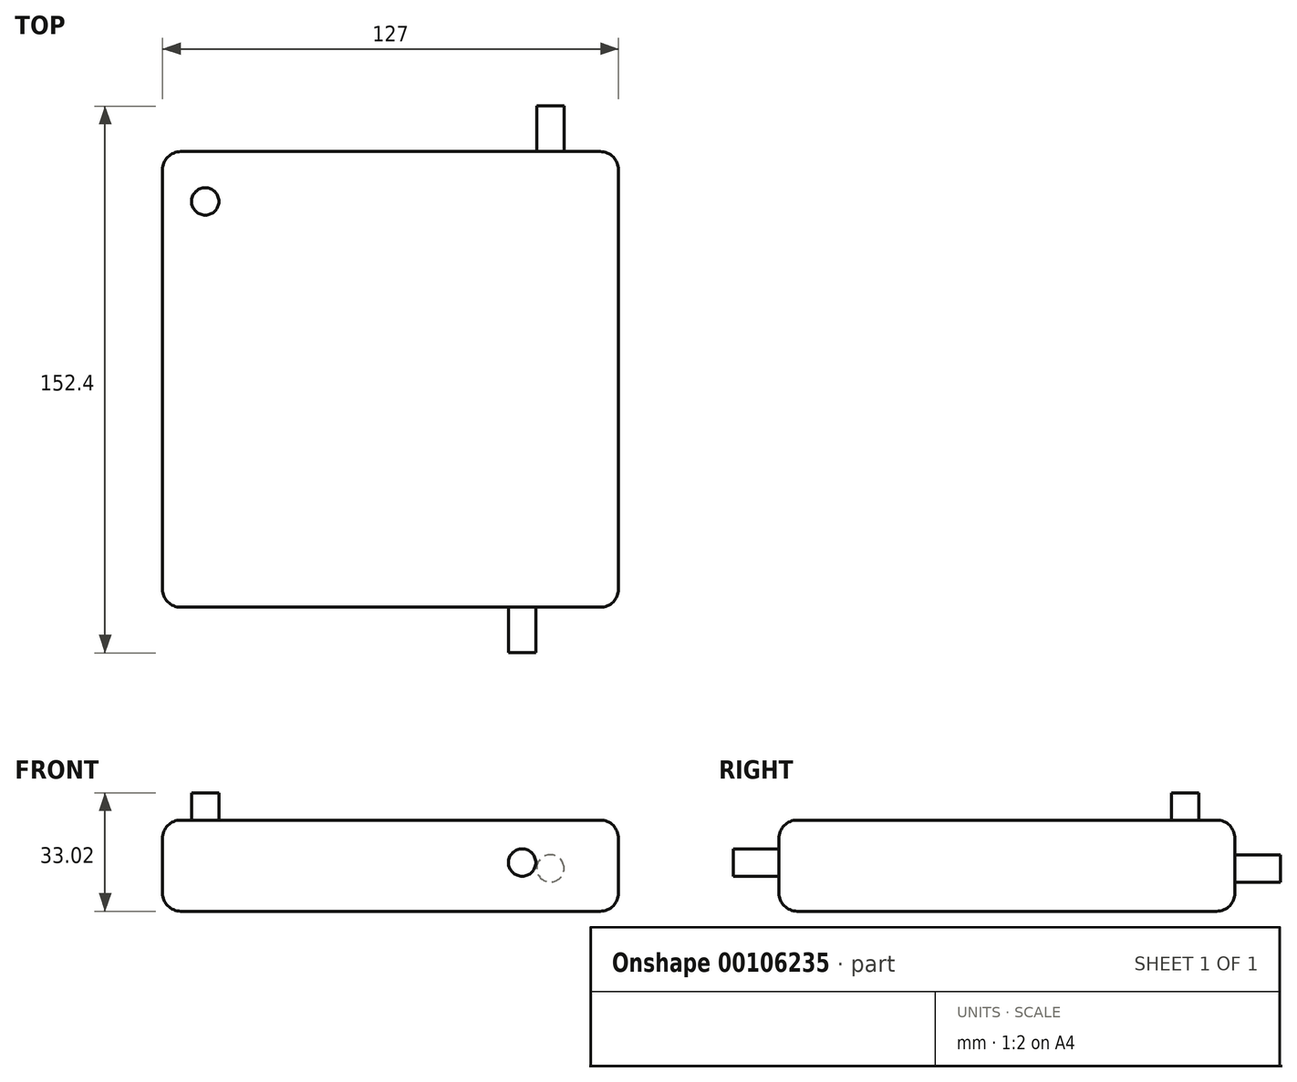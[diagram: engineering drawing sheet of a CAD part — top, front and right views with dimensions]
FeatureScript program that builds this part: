
annotation { "Feature Type Name" : "Feature", "Feature Type Description" : "" }
export const myFeature = defineFeature(function(context is Context, id is Id, definition is map)
    precondition{}
    {
        {
            var Q0;
            Q0=qCreatedBy(makeId("Top.planeOp"),FACE);
            var sketch = newSketch(context, id + "F0", { "sketchPlane" : qUnion([Q0])});
            skLineSegment(sketch, "E0.bottom", {"start": v(-67.6, 87.82) * mm, "end": v(59.4, 87.82) * mm});
            skLineSegment(sketch, "E0.top", {"start": v(-67.6, -39.18) * mm, "end": v(59.4, -39.18) * mm});
            skLineSegment(sketch, "E0.left", {"start": v(-67.6, 87.82) * mm, "end": v(-67.6, -39.18) * mm});
            skLineSegment(sketch, "E0.right", {"start": v(59.4, 87.82) * mm, "end": v(59.4, -39.18) * mm});
            skSolve(sketch);
        }
        {
            var Q0;
            Q0=makeQuery(id+"F0.imprint","IMPRINT",FACE,{"disambiguationData":[TD([[makeQuery(id+"F0.imprint","IMPRINT",EDGE,{"derivedFrom":sQuery(id+"F0.wireOp",EDGE,"E0.bottom")}),-1.0]])]});
            extrude(context, id + "F1", {"entities" : qUnion([Q0]), "depth" : 25.4 * mm});
        }
        {
            var Q0;
            Q0=makeQuery(id+"F1.opExtrude","CAP_FACE",FACE,{"disambiguationData":[OSD([sQuery(id+"F0.wireOp",EDGE,"E0.bottom"),sQuery(id+"F0.wireOp",EDGE,"E0.top"),sQuery(id+"F0.wireOp",EDGE,"E0.left"),sQuery(id+"F0.wireOp",EDGE,"E0.right")])],"isStart":false});
            var sketch = newSketch(context, id + "F2", { "sketchPlane" : qUnion([Q0])});
            skCircle(sketch, "E1", {"center": v(-55.71, 73.96) * mm, "radius": 3.81 * mm});
            skSolve(sketch);
        }
        {
            var Q0;
            Q0=makeQuery(id+"F2.imprint","IMPRINT",FACE,{"disambiguationData":[TD([[makeQuery(id+"F2.imprint","IMPRINT",EDGE,{"derivedFrom":sQuery(id+"F2.wireOp",EDGE,"E1")}),1.0]])]});
            var Q1;
            Q1=sQuery(id+"F2.wireOp",EDGE,"E1");
            extrude(context, id + "F3", {"entities" : qUnion([Q0]), "operationType" : NewBodyOperationType.ADD, "surfaceEntities" : qUnion([Q1]), "depth" : 7.62 * mm});
        }
        {
            var Q0;
            Q0=makeQuery(id+"F1.opExtrude","CAP_EDGE",EDGE,{"disambiguationData":[OSD([sQuery(id+"F0.wireOp",EDGE,"E0.right")])],"isStart":false});
            fillet(context, id + "F4", {"entities" : qUnion([Q0]), "radius" : 5.08 * mm, "tangentPropagation" : true, "allowEdgeOverflow" : false});
        }
        {
            var Q0;
            Q0=makeQuery(id+"F1.opExtrude","CAP_EDGE",EDGE,{"disambiguationData":[OSD([sQuery(id+"F0.wireOp",EDGE,"E0.top")])],"isStart":false});
            fillet(context, id + "F5", {"entities" : qUnion([Q0]), "radius" : 5.08 * mm, "tangentPropagation" : true, "allowEdgeOverflow" : false});
        }
        {
            var Q0;
            Q0=makeQuery(id+"F1.opExtrude","CAP_EDGE",EDGE,{"disambiguationData":[OSD([sQuery(id+"F0.wireOp",EDGE,"E0.left")])],"isStart":false});
            fillet(context, id + "F6", {"entities" : qUnion([Q0]), "radius" : 5.08 * mm, "tangentPropagation" : true, "allowEdgeOverflow" : false});
        }
        {
            var Q0;
            Q0=makeQuery(id+"F1.opExtrude","CAP_EDGE",EDGE,{"disambiguationData":[OSD([sQuery(id+"F0.wireOp",EDGE,"E0.bottom")])],"isStart":false});
            fillet(context, id + "F7", {"entities" : qUnion([Q0]), "radius" : 5.08 * mm, "tangentPropagation" : true, "allowEdgeOverflow" : false});
        }
        {
            var Q0;
            Q0=makeQuery(id+"F1.opExtrude","CAP_EDGE",EDGE,{"disambiguationData":[OSD([sQuery(id+"F0.wireOp",EDGE,"E0.right")])],"isStart":true});
            fillet(context, id + "F8", {"entities" : qUnion([Q0]), "radius" : 5.08 * mm, "tangentPropagation" : true, "allowEdgeOverflow" : false});
        }
        {
            var Q0;
            Q0=makeQuery(id+"F1.opExtrude","SWEPT_FACE",FACE,{"disambiguationData":[OSD([sQuery(id+"F0.wireOp",EDGE,"E0.top")])]});
            var sketch = newSketch(context, id + "F9", { "sketchPlane" : qUnion([Q0])});
            skCircle(sketch, "E2", {"center": v(32.56, 13.58) * mm, "radius": 3.81 * mm});
            skSolve(sketch);
        }
        {
            var Q0;
            Q0=makeQuery(id+"F9.imprint","IMPRINT",FACE,{"disambiguationData":[TD([[makeQuery(id+"F9.imprint","IMPRINT",EDGE,{"derivedFrom":sQuery(id+"F9.wireOp",EDGE,"E2")}),1.0]])]});
            var Q1;
            Q1=sQuery(id+"F9.wireOp",EDGE,"E2");
            extrude(context, id + "F10", {"entities" : qUnion([Q0]), "operationType" : NewBodyOperationType.ADD, "surfaceEntities" : qUnion([Q1]), "depth" : 12.7 * mm});
        }
        {
            var Q0;
            Q0=makeQuery(id+"F1.opExtrude","SWEPT_FACE",FACE,{"disambiguationData":[OSD([sQuery(id+"F0.wireOp",EDGE,"E0.bottom")])]});
            var sketch = newSketch(context, id + "F11", { "sketchPlane" : qUnion([Q0])});
            skCircle(sketch, "E3", {"center": v(-40.41, 11.94) * mm, "radius": 3.81 * mm});
            skSolve(sketch);
        }
        {
            var Q0;
            Q0=makeQuery(id+"F11.imprint","IMPRINT",FACE,{"disambiguationData":[TD([[makeQuery(id+"F11.imprint","IMPRINT",EDGE,{"derivedFrom":sQuery(id+"F11.wireOp",EDGE,"E3")}),1.0]])]});
            extrude(context, id + "F12", {"entities" : qUnion([Q0]), "operationType" : NewBodyOperationType.ADD, "depth" : 12.7 * mm});
        }
    });
